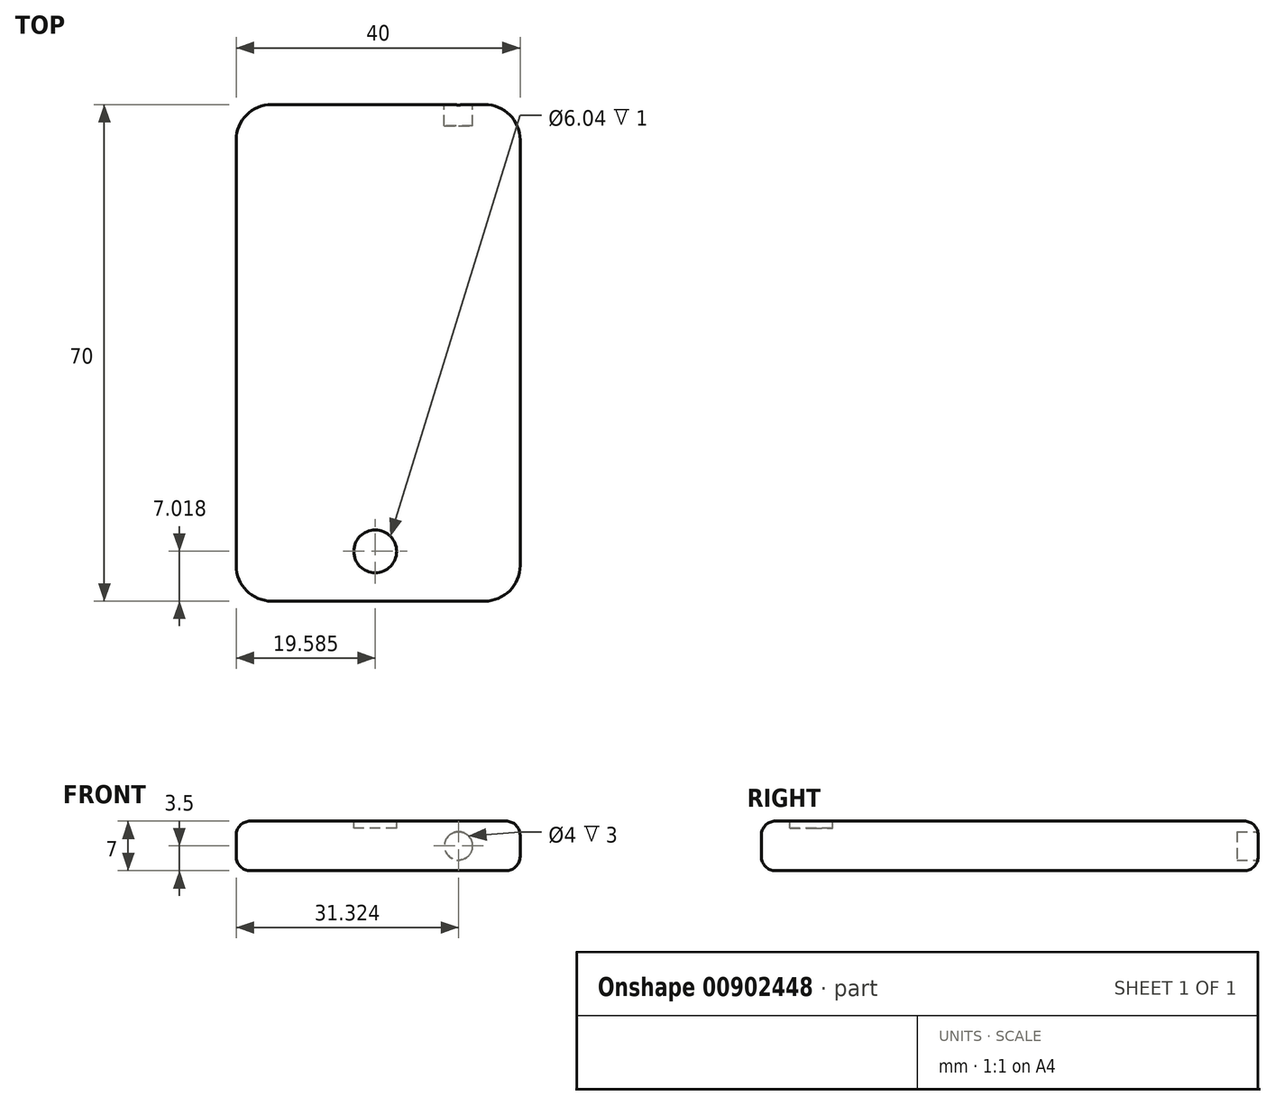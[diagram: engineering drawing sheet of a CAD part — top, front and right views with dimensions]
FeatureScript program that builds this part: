
annotation { "Feature Type Name" : "Feature", "Feature Type Description" : "" }
export const myFeature = defineFeature(function(context is Context, id is Id, definition is map)
    precondition{}
    {
        {
            var Q0;
            Q0=qCreatedBy(makeId("Top.planeOp"),FACE);
            var sketch = newSketch(context, id + "F0", { "sketchPlane" : qUnion([Q0])});
            skLineSegment(sketch, "E0.bottom", {"start": v(0, 70) * mm, "end": v(40, 70) * mm});
            skLineSegment(sketch, "E0.top", {"start": v(0, 0) * mm, "end": v(40, 0) * mm});
            skLineSegment(sketch, "E0.left", {"start": v(0, 70) * mm, "end": v(0, 0) * mm});
            skLineSegment(sketch, "E0.right", {"start": v(40, 70) * mm, "end": v(40, 0) * mm});
            skSolve(sketch);
        }
        {
            var Q0;
            Q0=makeQuery(id+"F0.imprint","IMPRINT",FACE,{"disambiguationData":[TD([[makeQuery(id+"F0.imprint","IMPRINT",EDGE,{"derivedFrom":sQuery(id+"F0.wireOp",EDGE,"E0.bottom")}),-1.0]])]});
            extrude(context, id + "F1", {"entities" : qUnion([Q0]), "depth" : 7 * mm, "offsetDistance" : 25 * mm});
        }
        {
            var Q0;
            Q0=makeQuery(id+"F1.opExtrude","SWEPT_EDGE",EDGE,{"disambiguationData":[OSD([sQuery(id+"F0.wireOp",EDGE,"E0.top"),sQuery(id+"F0.wireOp",EDGE,"E0.right")])]});
            var Q1;
            Q1=makeQuery(id+"F1.opExtrude","SWEPT_EDGE",EDGE,{"disambiguationData":[OSD([sQuery(id+"F0.wireOp",EDGE,"E0.bottom"),sQuery(id+"F0.wireOp",EDGE,"E0.right")])]});
            var Q2;
            Q2=makeQuery(id+"F1.opExtrude","SWEPT_EDGE",EDGE,{"disambiguationData":[OSD([sQuery(id+"F0.wireOp",EDGE,"E0.bottom"),sQuery(id+"F0.wireOp",EDGE,"E0.left")])]});
            var Q3;
            Q3=makeQuery(id+"F1.opExtrude","SWEPT_EDGE",EDGE,{"disambiguationData":[OSD([sQuery(id+"F0.wireOp",EDGE,"E0.top"),sQuery(id+"F0.wireOp",EDGE,"E0.left")])]});
            fillet(context, id + "F2", {"entities" : qUnion([Q0, Q1, Q2, Q3]), "radius" : 5 * mm, "tangentPropagation" : true, "allowEdgeOverflow" : false});
        }
        {
            var Q0;
            Q0=makeQuery(id+"F1.opExtrude","SWEPT_FACE",FACE,{"disambiguationData":[OSD([sQuery(id+"F0.wireOp",EDGE,"E0.bottom")])]});
            var sketch = newSketch(context, id + "F3", { "sketchPlane" : qUnion([Q0])});
            skCircle(sketch, "E1", {"center": v(-31.32, 3.5) * mm, "radius": 2 * mm});
            skPoint(sketch, "E1.centerSnap0", {"position": v(-35, 3.5) * mm});
            skSolve(sketch);
        }
        {
            var Q0;
            Q0=makeQuery(id+"F3.imprint","IMPRINT",FACE,{"disambiguationData":[TD([[makeQuery(id+"F3.imprint","IMPRINT",EDGE,{"derivedFrom":sQuery(id+"F3.wireOp",EDGE,"E1")}),1.0]])]});
            extrude(context, id + "F4", {"entities" : qUnion([Q0]), "operationType" : NewBodyOperationType.REMOVE, "oppositeDirection" : true, "depth" : 3 * mm, "offsetDistance" : 25 * mm});
        }
        {
            var Q0;
            Q0=makeQuery(id+"F1.opExtrude","CAP_EDGE",EDGE,{"disambiguationData":[OSD([sQuery(id+"F0.wireOp",EDGE,"E0.left")])],"isStart":true});
            fillet(context, id + "F5", {"entities" : qUnion([Q0]), "radius" : 2 * mm, "tangentPropagation" : true, "allowEdgeOverflow" : false});
        }
        {
            var Q0;
            Q0=makeQuery(id+"F1.opExtrude","CAP_EDGE",EDGE,{"disambiguationData":[OSD([sQuery(id+"F0.wireOp",EDGE,"E0.left")])],"isStart":false});
            fillet(context, id + "F6", {"entities" : qUnion([Q0]), "radius" : 2 * mm, "tangentPropagation" : true, "allowEdgeOverflow" : false});
        }
        {
            var Q0;
            Q0=makeQuery(id+"F1.opExtrude","CAP_FACE",FACE,{"disambiguationData":[OSD([sQuery(id+"F0.wireOp",EDGE,"E0.bottom"),sQuery(id+"F0.wireOp",EDGE,"E0.top"),sQuery(id+"F0.wireOp",EDGE,"E0.left"),sQuery(id+"F0.wireOp",EDGE,"E0.right")])],"isStart":false});
            var sketch = newSketch(context, id + "F7", { "sketchPlane" : qUnion([Q0])});
            skCircle(sketch, "E2", {"center": v(19.59, 7.02) * mm, "radius": 3.02 * mm});
            skSolve(sketch);
        }
        {
            var Q0;
            Q0 = qSketchRegion(id + "F7", true);
            extrude(context, id + "F8", {"entities" : qUnion([Q0]), "operationType" : NewBodyOperationType.REMOVE, "oppositeDirection" : true, "depth" : 1 * mm, "offsetDistance" : 25 * mm});
        }
    });
